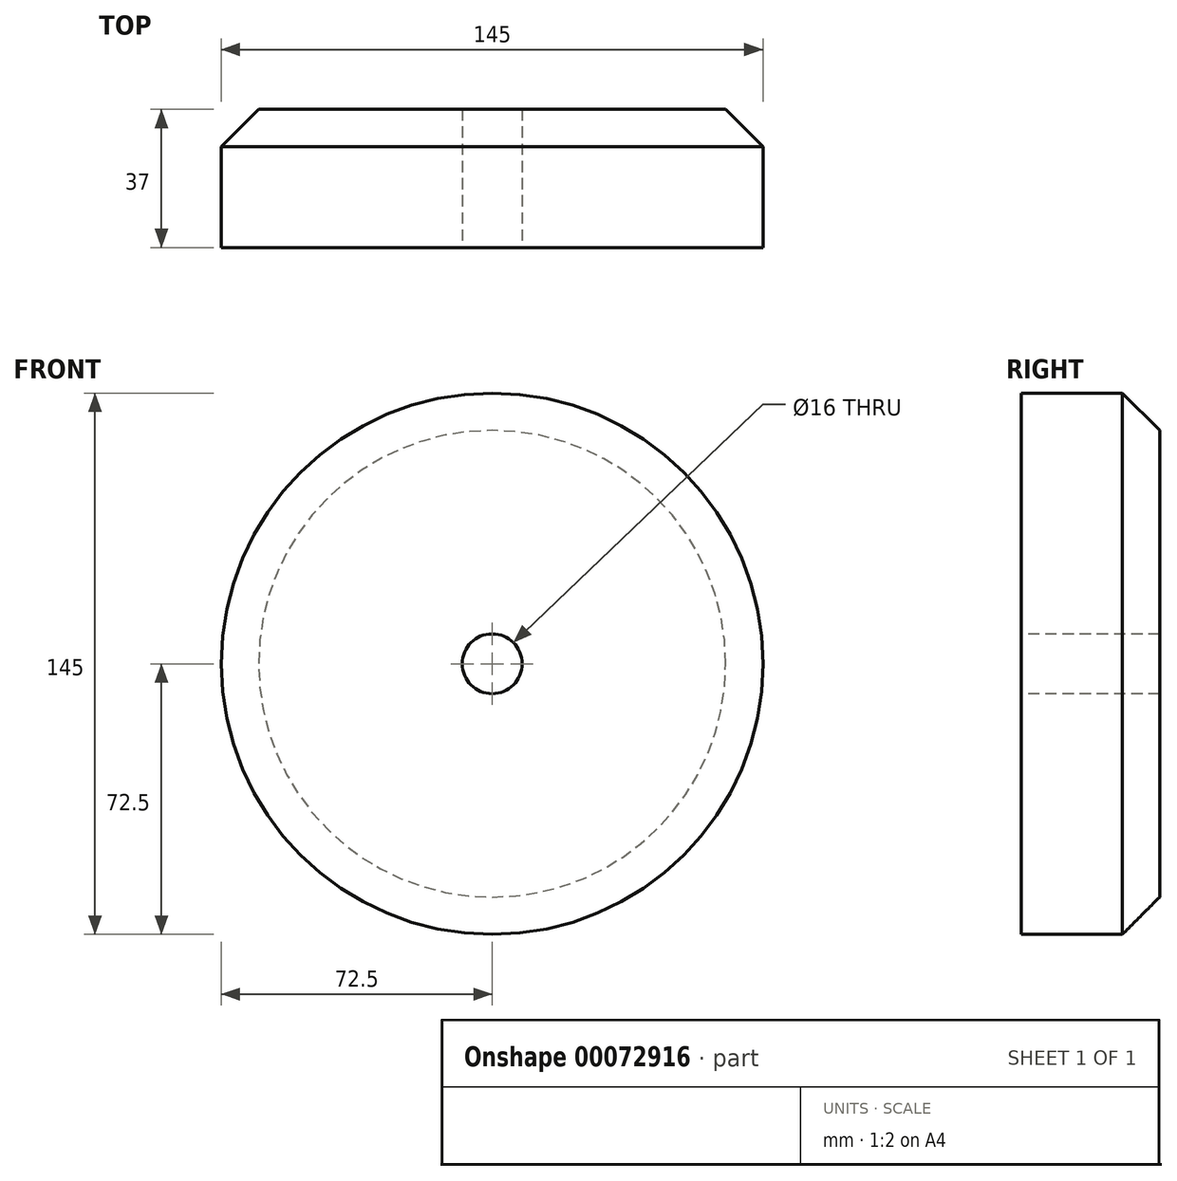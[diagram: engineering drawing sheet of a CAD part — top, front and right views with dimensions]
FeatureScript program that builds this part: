
annotation { "Feature Type Name" : "Feature", "Feature Type Description" : "" }
export const myFeature = defineFeature(function(context is Context, id is Id, definition is map)
    precondition{}
    {
        {
            var Q0;
            Q0=qCreatedBy(makeId("Front.planeOp"),FACE);
            var sketch = newSketch(context, id + "F0", { "sketchPlane" : qUnion([Q0])});
            skCircle(sketch, "E0", {"center": v(0, 0) * mm, "radius": 72.5 * mm});
            skCircle(sketch, "E1", {"center": v(0, 0) * mm, "radius": 8 * mm});
            skSolve(sketch);
        }
        {
            var Q0;
            Q0 = qSketchRegion(id + "F0", true);
            extrude(context, id + "F1", {"entities" : qUnion([Q0]), "oppositeDirection" : true, "depth" : 37 * mm});
        }
        {
            var Q0;
            Q0=makeQuery(id+"F1.opExtrude","CAP_EDGE",EDGE,{"disambiguationData":[OSD([sQuery(id+"F0.wireOp",EDGE,"E0")])],"isStart":false});
            chamfer(context, id + "F2", {"entities" : qUnion([Q0]), "width" : 10 * mm, "tangentPropagation" : true});
        }
    });
